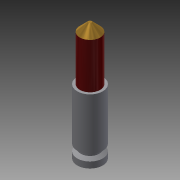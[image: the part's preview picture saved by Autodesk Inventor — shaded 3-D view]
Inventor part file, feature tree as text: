
AUTODESK INVENTOR PART (.ipt)
format: ipt  version: 2013 (Build 170138000, 138)  size: 97,280 bytes
history: native  units: mm
features: revolve x1, sketch x1
ambient origin geometry x8: Origin, YZ Plane, XZ Plane, XY Plane, X Axis, Y Axis, Z Axis, Center Point
bodies: Solid1 (feature_tree)
feature tree (2):
  revolve  "Revolution1"  [1 undecoded]
  sketch  "Sketch1"  dims[d1=3.81mm d3=74.041mm d4=32.258mm d5=0.762mm d6=1.524mm d7=4.191mm d8=5.842mm d9=7.9629mm d10=6.3754mm d11=45.0deg d12=1.0mm d13=90.0deg]
note: 1 required parameter value undecoded (feature->parameter linkage not recoverable at this tier; creation-order binding heuristic only, values carry confidence <= 0.55)
